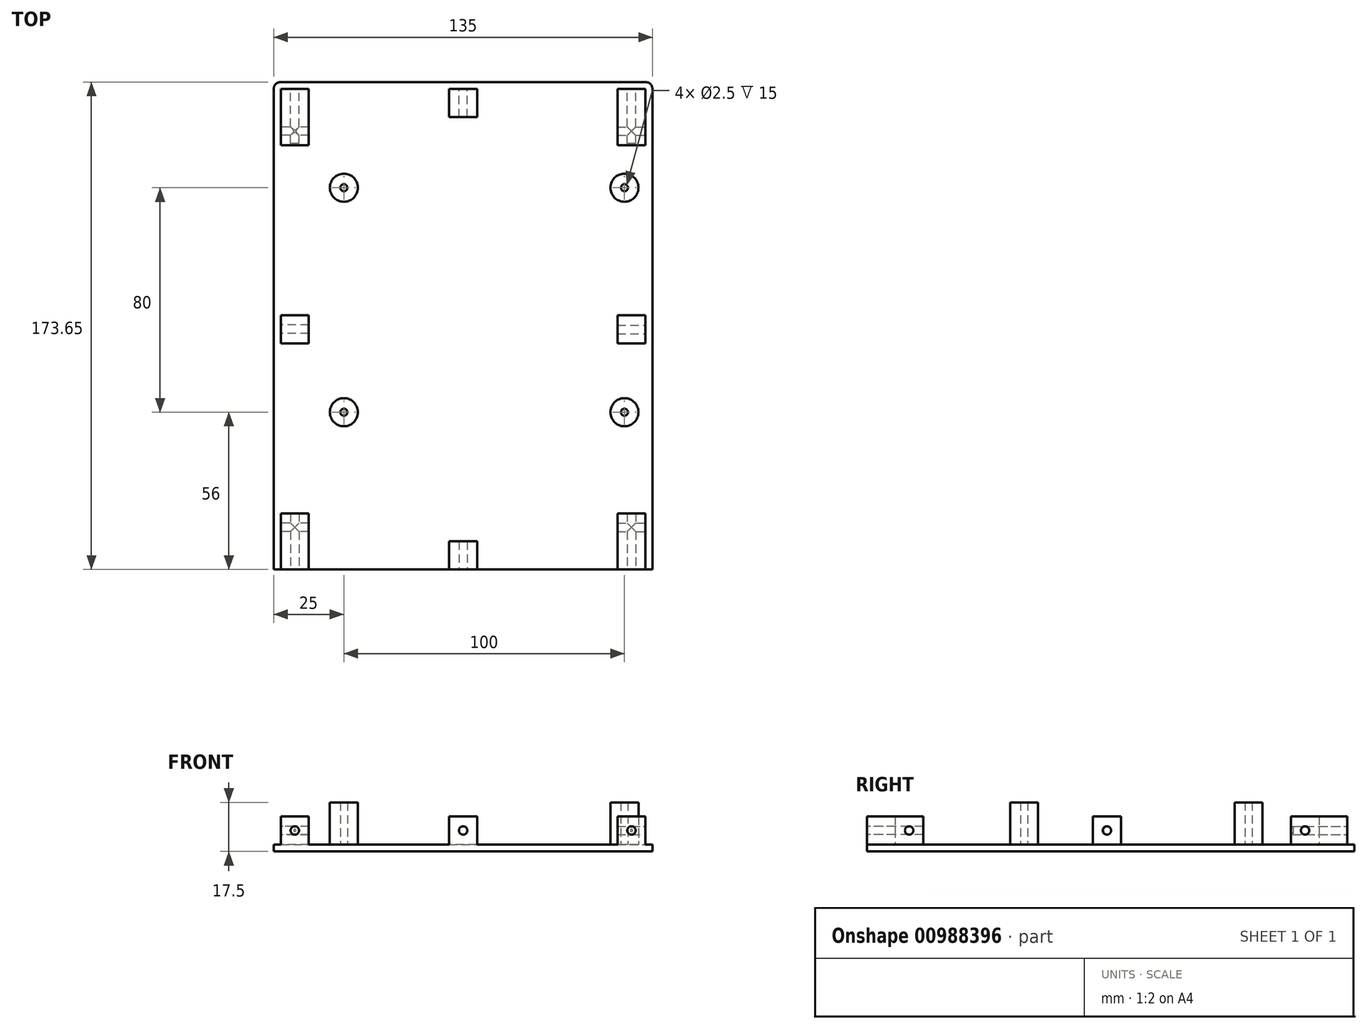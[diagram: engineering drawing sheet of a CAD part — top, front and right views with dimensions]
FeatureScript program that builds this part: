
annotation { "Feature Type Name" : "Feature", "Feature Type Description" : "" }
export const myFeature = defineFeature(function(context is Context, id is Id, definition is map)
    precondition{}
    {
        {
            var Q0;
            Q0=qCreatedBy(makeId("Top.planeOp"),FACE);
            cPlane(context, id + "F0", {"entities" : qUnion([Q0]), "cplaneType" : CPlaneType.OFFSET, "offset" : 7.5 * mm, "oppositeDirection" : true, "width" : 150 * mm, "height" : 150 * mm});
        }
        {
            var Q0;
            Q0=qCreatedBy(id+"F0.planeOp",FACE);
            var sketch = newSketch(context, id + "F1", { "sketchPlane" : qUnion([Q0])});
            skLineSegment(sketch, "E0.bottom", {"start": v(-67.5, -86.82) * mm, "end": v(67.5, -86.82) * mm});
            skLineSegment(sketch, "E0.top", {"start": v(-67.5, 86.83) * mm, "end": v(67.5, 86.83) * mm});
            skLineSegment(sketch, "E0.left", {"start": v(-67.5, -86.82) * mm, "end": v(-67.5, 86.83) * mm});
            skLineSegment(sketch, "E0.right", {"start": v(67.5, -86.82) * mm, "end": v(67.5, 86.83) * mm});
            skPoint(sketch, "E1", {"position": v(-67.5, -86.82) * mm});
            skPoint(sketch, "E2", {"position": v(67.5, 86.83) * mm});
            skSolve(sketch);
        }
        {
            var Q0;
            Q0 = qSketchRegion(id + "F1", true);
            extrude(context, id + "F2", {"entities" : qUnion([Q0]), "endBound" : BoundingType.SYMMETRIC, "depth" : 2.5 * mm, "offsetDistance" : 25 * mm});
        }
        {
            var Q0;
            Q0=qCreatedBy(id+"F0.planeOp",FACE);
            var sketch = newSketch(context, id + "F3", { "sketchPlane" : qUnion([Q0])});
            skLineSegment(sketch, "E3", {"start": v(0, 88.08) * mm, "end": v(0, -86.8) * mm, "construction": true});
            skLineSegment(sketch, "E4.bottom", {"start": v(-65, -6.27) * mm, "end": v(-55, -6.27) * mm});
            skLineSegment(sketch, "E4.top", {"start": v(-65, 3.73) * mm, "end": v(-55, 3.73) * mm});
            skLineSegment(sketch, "E4.left", {"start": v(-65, -6.27) * mm, "end": v(-65, 3.73) * mm});
            skLineSegment(sketch, "E4.right", {"start": v(-55, -6.27) * mm, "end": v(-55, 3.73) * mm});
            skLineSegment(sketch, "E5.bottom", {"start": v(-5, 84.33) * mm, "end": v(5, 84.33) * mm});
            skLineSegment(sketch, "E5.top", {"start": v(-5, 74.33) * mm, "end": v(5, 74.33) * mm});
            skLineSegment(sketch, "E5.left", {"start": v(-5, 84.33) * mm, "end": v(-5, 74.33) * mm});
            skLineSegment(sketch, "E5.right", {"start": v(5, 84.33) * mm, "end": v(5, 74.33) * mm});
            skLineSegment(sketch, "E6.bottom", {"start": v(-65, 84.33) * mm, "end": v(-55, 84.33) * mm});
            skLineSegment(sketch, "E6.top", {"start": v(-65, 64.33) * mm, "end": v(-55, 64.33) * mm});
            skLineSegment(sketch, "E6.left", {"start": v(-65, 84.33) * mm, "end": v(-65, 64.33) * mm});
            skLineSegment(sketch, "E6.right", {"start": v(-55, 84.33) * mm, "end": v(-55, 64.33) * mm});
            skLineSegment(sketch, "E7.bottom", {"start": v(-65, -66.82) * mm, "end": v(-55, -66.82) * mm});
            skLineSegment(sketch, "E7.top", {"start": v(-65, -86.82) * mm, "end": v(-55, -86.82) * mm});
            skLineSegment(sketch, "E7.left", {"start": v(-65, -66.82) * mm, "end": v(-65, -86.82) * mm});
            skLineSegment(sketch, "E7.right", {"start": v(-55, -66.82) * mm, "end": v(-55, -86.82) * mm});
            skLineSegment(sketch, "E8.bottom", {"start": v(-5, -86.82) * mm, "end": v(5, -86.82) * mm});
            skLineSegment(sketch, "E8.top", {"start": v(-5, -76.82) * mm, "end": v(5, -76.82) * mm});
            skLineSegment(sketch, "E8.left", {"start": v(-5, -86.82) * mm, "end": v(-5, -76.82) * mm});
            skLineSegment(sketch, "E8.right", {"start": v(5, -86.82) * mm, "end": v(5, -76.82) * mm});
            skLineSegment(sketch, "E9.MirrorCS", {"start": v(65, -6.27) * mm, "end": v(65, 3.73) * mm});
            skLineSegment(sketch, "E10.MirrorCS", {"start": v(65, 64.33) * mm, "end": v(55, 64.33) * mm});
            skLineSegment(sketch, "E11.MirrorCS", {"start": v(65, -6.27) * mm, "end": v(55, -6.27) * mm});
            skLineSegment(sketch, "E12.MirrorCS", {"start": v(65, -66.82) * mm, "end": v(55, -66.82) * mm});
            skLineSegment(sketch, "E13.MirrorCS", {"start": v(55, -6.27) * mm, "end": v(55, 3.73) * mm});
            skLineSegment(sketch, "E14.MirrorCS", {"start": v(65, 3.73) * mm, "end": v(55, 3.73) * mm});
            skLineSegment(sketch, "E15.MirrorCS", {"start": v(65, 84.33) * mm, "end": v(55, 84.33) * mm});
            skLineSegment(sketch, "E16.MirrorCS", {"start": v(65, -86.82) * mm, "end": v(55, -86.82) * mm});
            skLineSegment(sketch, "E17.MirrorCS", {"start": v(65, 84.33) * mm, "end": v(65, 64.33) * mm});
            skLineSegment(sketch, "E18.MirrorCS", {"start": v(65, -66.82) * mm, "end": v(65, -86.82) * mm});
            skLineSegment(sketch, "E19.MirrorCS", {"start": v(55, -66.82) * mm, "end": v(55, -86.82) * mm});
            skLineSegment(sketch, "E20.MirrorCS", {"start": v(55, 84.33) * mm, "end": v(55, 64.33) * mm});
            skSolve(sketch);
        }
        {
            var Q0;
            Q0 = qSketchRegion(id + "F3", true);
            extrude(context, id + "F4", {"entities" : qUnion([Q0]), "operationType" : NewBodyOperationType.ADD, "depth" : 11.25 * mm, "offsetDistance" : 25 * mm});
        }
        {
            var Q0;
            Q0=qCreatedBy(id+"F0.planeOp",FACE);
            var sketch = newSketch(context, id + "F5", { "sketchPlane" : qUnion([Q0])});
            skCircle(sketch, "E21", {"center": v(-42.5, 49.18) * mm, "radius": 1.25 * mm});
            skCircle(sketch, "E22", {"center": v(-42.5, 49.18) * mm, "radius": 5 * mm});
            skCircle(sketch, "E23", {"center": v(-42.5, -30.82) * mm, "radius": 1.25 * mm});
            skCircle(sketch, "E24", {"center": v(-42.5, -30.82) * mm, "radius": 5 * mm});
            skCircle(sketch, "E25", {"center": v(57.5, -30.82) * mm, "radius": 1.25 * mm});
            skCircle(sketch, "E26", {"center": v(57.5, -30.82) * mm, "radius": 5 * mm});
            skCircle(sketch, "E27", {"center": v(57.5, 49.18) * mm, "radius": 1.25 * mm});
            skCircle(sketch, "E28", {"center": v(57.5, 49.18) * mm, "radius": 5 * mm});
            skSolve(sketch);
        }
        {
            var Q0;
            Q0 = qSketchRegion(id + "F5", true);
            extrude(context, id + "F6", {"entities" : qUnion([Q0]), "operationType" : NewBodyOperationType.ADD, "depth" : 16.25 * mm, "offsetDistance" : 25 * mm});
        }
        {
            var Q0;
            Q0=makeQuery(id+"F2.opExtrude","SWEPT_EDGE",EDGE,{"disambiguationData":[OSD([sQuery(id+"F1.wireOp",EDGE,"E0.top"),sQuery(id+"F1.wireOp",EDGE,"E0.left")])]});
            var Q1;
            Q1=makeQuery(id+"F2.opExtrude","SWEPT_EDGE",EDGE,{"disambiguationData":[OSD([sQuery(id+"F1.wireOp",EDGE,"E0.top"),sQuery(id+"F1.wireOp",EDGE,"E0.right")])]});
            fillet(context, id + "F7", {"entities" : qUnion([Q0, Q1]), "radius" : 2.5 * mm, "tangentPropagation" : true, "allowEdgeOverflow" : false});
        }
        {
            var Q0;
            Q0=qCreatedBy(makeId("Front.planeOp"),FACE);
            cPlane(context, id + "F8", {"entities" : qUnion([Q0]), "cplaneType" : CPlaneType.OFFSET, "offset" : 88 * mm, "width" : 150 * mm, "height" : 150 * mm});
        }
        {
            var Q0;
            Q0=qCreatedBy(id+"F8.planeOp",FACE);
            var sketch = newSketch(context, id + "F9", { "sketchPlane" : qUnion([Q0])});
            skPoint(sketch, "E29", {"position": v(-60, -1.25) * mm});
            skPoint(sketch, "E30", {"position": v(0, -1.25) * mm});
            skPoint(sketch, "E31", {"position": v(60, -1.25) * mm});
            skSolve(sketch);
        }
        {
            var Q0;
            Q0=qCreatedBy(makeId("Front.planeOp"),FACE);
            cPlane(context, id + "F10", {"entities" : qUnion([Q0]), "cplaneType" : CPlaneType.OFFSET, "offset" : 90 * mm, "oppositeDirection" : true, "width" : 150 * mm, "height" : 150 * mm});
        }
        {
            var Q0;
            Q0=qCreatedBy(id+"F10.planeOp",FACE);
            var sketch = newSketch(context, id + "F11", { "sketchPlane" : qUnion([Q0])});
            skPoint(sketch, "E32", {"position": v(60, -1.25) * mm});
            skPoint(sketch, "E33", {"position": v(0, -1.25) * mm});
            skPoint(sketch, "E34", {"position": v(-60, -1.25) * mm});
            skSolve(sketch);
        }
        {
            var Q0;
            Q0=qCreatedBy(makeId("Right.planeOp"),FACE);
            cPlane(context, id + "F12", {"entities" : qUnion([Q0]), "cplaneType" : CPlaneType.OFFSET, "offset" : 70.5 * mm, "oppositeDirection" : true, "width" : 150 * mm, "height" : 150 * mm});
        }
        {
            var Q0;
            Q0=qCreatedBy(id+"F12.planeOp",FACE);
            var sketch = newSketch(context, id + "F13", { "sketchPlane" : qUnion([Q0])});
            skPoint(sketch, "E35", {"position": v(69.33, -1.3) * mm});
            skPoint(sketch, "E36", {"position": v(-1.23, -1.25) * mm});
            skPoint(sketch, "E37", {"position": v(-71.82, -1.25) * mm});
            skSolve(sketch);
        }
        {
            var Q0;
            Q0=qCreatedBy(makeId("Right.planeOp"),FACE);
            cPlane(context, id + "F14", {"entities" : qUnion([Q0]), "cplaneType" : CPlaneType.OFFSET, "offset" : 70 * mm, "width" : 150 * mm, "height" : 150 * mm});
        }
        {
            var Q0;
            Q0=qCreatedBy(id+"F14.planeOp",FACE);
            var sketch = newSketch(context, id + "F15", { "sketchPlane" : qUnion([Q0])});
            skPoint(sketch, "E38", {"position": v(-71.82, -1.25) * mm});
            skPoint(sketch, "E39", {"position": v(-1.32, -1.25) * mm});
            skPoint(sketch, "E40", {"position": v(69.33, -1.25) * mm});
            skSolve(sketch);
        }
        {
            var Q0;
            Q0=sQuery(id+"F9.wireOp",VERTEX,"E29");
            var Q1;
            Q1=sQuery(id+"F9.wireOp",VERTEX,"E30");
            var Q2;
            Q2=sQuery(id+"F9.wireOp",VERTEX,"E31");
            var Q3;
            Q3=makeQuery(id+"F2.opExtrude","SWEPT_BODY",BODY,{"disambiguationData":[OSD([sQuery(id+"F1.wireOp",EDGE,"E0.bottom"),sQuery(id+"F1.wireOp",EDGE,"E0.top"),sQuery(id+"F1.wireOp",EDGE,"E0.left"),sQuery(id+"F1.wireOp",EDGE,"E0.right")])]});
            hole(context, id + "F16", {"style" : HoleStyle.SIMPLE, "endStyle" : HoleEndStyle.BLIND, "holeDiameter" : 3 * mm, "majorDiameter" : 5 * mm, "holeDepth" : 25 * mm, "isTappedThrough" : true, "tappedDepth" : 12 * mm, "tapClearance" : 3, "startFromSketch" : true, "locations" : qUnion([Q0, Q1, Q2]), "scope" : qUnion([Q3])});
        }
        {
            var Q0;
            Q0=sQuery(id+"F15.wireOp",VERTEX,"E38");
            var Q1;
            Q1=sQuery(id+"F15.wireOp",VERTEX,"E39");
            var Q2;
            Q2=sQuery(id+"F15.wireOp",VERTEX,"E40");
            var Q3;
            Q3=makeQuery(id+"F2.opExtrude","SWEPT_BODY",BODY,{"disambiguationData":[OSD([sQuery(id+"F1.wireOp",EDGE,"E0.bottom"),sQuery(id+"F1.wireOp",EDGE,"E0.top"),sQuery(id+"F1.wireOp",EDGE,"E0.left"),sQuery(id+"F1.wireOp",EDGE,"E0.right")])]});
            hole(context, id + "F17", {"style" : HoleStyle.SIMPLE, "endStyle" : HoleEndStyle.BLIND, "holeDiameter" : 3 * mm, "majorDiameter" : 5 * mm, "holeDepth" : 25 * mm, "isTappedThrough" : true, "tappedDepth" : 12 * mm, "tapClearance" : 3, "startFromSketch" : true, "locations" : qUnion([Q0, Q1, Q2]), "scope" : qUnion([Q3])});
        }
        {
            var Q0;
            Q0=sQuery(id+"F11.wireOp",VERTEX,"E32");
            var Q1;
            Q1=sQuery(id+"F11.wireOp",VERTEX,"E33");
            var Q2;
            Q2=sQuery(id+"F11.wireOp",VERTEX,"E34");
            var Q3;
            Q3=makeQuery(id+"F2.opExtrude","SWEPT_BODY",BODY,{"disambiguationData":[OSD([sQuery(id+"F1.wireOp",EDGE,"E0.bottom"),sQuery(id+"F1.wireOp",EDGE,"E0.top"),sQuery(id+"F1.wireOp",EDGE,"E0.left"),sQuery(id+"F1.wireOp",EDGE,"E0.right")])]});
            hole(context, id + "F18", {"style" : HoleStyle.SIMPLE, "endStyle" : HoleEndStyle.BLIND, "oppositeDirection" : true, "holeDiameter" : 3 * mm, "majorDiameter" : 5 * mm, "holeDepth" : 25 * mm, "isTappedThrough" : true, "tappedDepth" : 12 * mm, "tapClearance" : 3, "startFromSketch" : true, "locations" : qUnion([Q0, Q1, Q2]), "scope" : qUnion([Q3])});
        }
        {
            var Q0;
            Q0=sQuery(id+"F13.wireOp",VERTEX,"E35");
            var Q1;
            Q1=sQuery(id+"F13.wireOp",VERTEX,"E36");
            var Q2;
            Q2=sQuery(id+"F13.wireOp",VERTEX,"E37");
            var Q3;
            Q3=makeQuery(id+"F2.opExtrude","SWEPT_BODY",BODY,{"disambiguationData":[OSD([sQuery(id+"F1.wireOp",EDGE,"E0.bottom"),sQuery(id+"F1.wireOp",EDGE,"E0.top"),sQuery(id+"F1.wireOp",EDGE,"E0.left"),sQuery(id+"F1.wireOp",EDGE,"E0.right")])]});
            hole(context, id + "F19", {"style" : HoleStyle.SIMPLE, "endStyle" : HoleEndStyle.BLIND, "oppositeDirection" : true, "holeDiameter" : 3 * mm, "majorDiameter" : 5 * mm, "holeDepth" : 25 * mm, "isTappedThrough" : true, "tappedDepth" : 12 * mm, "tapClearance" : 3, "startFromSketch" : true, "locations" : qUnion([Q0, Q1, Q2]), "scope" : qUnion([Q3])});
        }
    });
